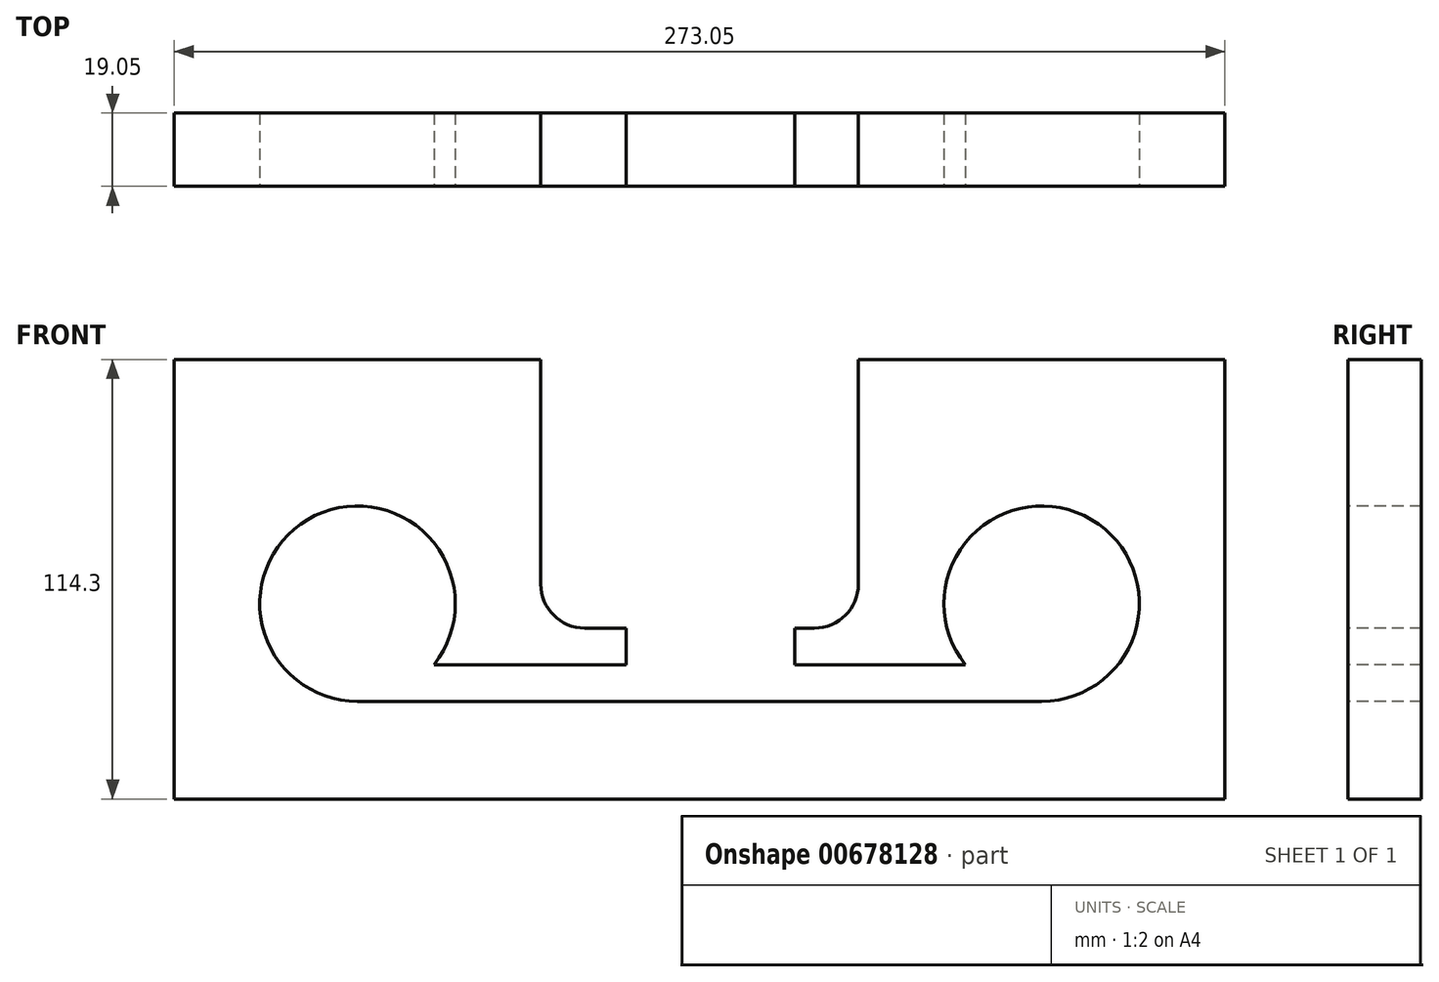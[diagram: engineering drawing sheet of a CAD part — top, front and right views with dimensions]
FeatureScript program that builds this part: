
annotation { "Feature Type Name" : "Feature", "Feature Type Description" : "" }
export const myFeature = defineFeature(function(context is Context, id is Id, definition is map)
    precondition{}
    {
        {
            var Q0;
            Q0=qCreatedBy(makeId("Front.planeOp"),FACE);
            var sketch = newSketch(context, id + "F0", { "sketchPlane" : qUnion([Q0])});
            skLineSegment(sketch, "E0.bottom", {"start": v(0, 0) * mm, "end": v(273.05, 0) * mm});
            skLineSegment(sketch, "E0.top", {"start": v(0, 114.3) * mm, "end": v(273.05, 114.3) * mm});
            skLineSegment(sketch, "E0.left", {"start": v(0, 0) * mm, "end": v(0, 114.3) * mm});
            skLineSegment(sketch, "E0.right", {"start": v(273.05, 0) * mm, "end": v(273.05, 114.3) * mm});
            skSolve(sketch);
        }
        {
            var Q0;
            Q0 = qSketchRegion(id + "F0", true);
            extrude(context, id + "F1", {"entities" : qUnion([Q0]), "depth" : 19.05 * mm, "offsetDistance" : 25.4 * mm});
        }
        {
            var Q0;
            Q0=makeQuery(id+"F1.opExtrude","CAP_FACE",FACE,{"disambiguationData":[OSD([sQuery(id+"F0.wireOp",EDGE,"E0.bottom"),sQuery(id+"F0.wireOp",EDGE,"E0.top"),sQuery(id+"F0.wireOp",EDGE,"E0.left"),sQuery(id+"F0.wireOp",EDGE,"E0.right")])],"isStart":false});
            var sketch = newSketch(context, id + "F2", { "sketchPlane" : qUnion([Q0])});
            skCircle(sketch, "E1", {"center": v(47.63, 50.8) * mm, "radius": 25.4 * mm});
            skCircle(sketch, "E2", {"center": v(225.43, 50.8) * mm, "radius": 25.4 * mm});
            skSolve(sketch);
        }
        {
            var Q0;
            Q0=makeQuery(id+"F2.imprint","IMPRINT",FACE,{"disambiguationData":[TD([[makeQuery(id+"F2.imprint","IMPRINT",EDGE,{"derivedFrom":sQuery(id+"F2.wireOp",EDGE,"E2")}),1.0]])]});
            var Q1;
            Q1=makeQuery(id+"F2.imprint","IMPRINT",FACE,{"disambiguationData":[TD([[makeQuery(id+"F2.imprint","IMPRINT",EDGE,{"derivedFrom":sQuery(id+"F2.wireOp",EDGE,"E1")}),1.0]])]});
            extrude(context, id + "F3", {"entities" : qUnion([Q0, Q1]), "operationType" : NewBodyOperationType.REMOVE, "oppositeDirection" : true, "depth" : 25.4 * mm, "offsetDistance" : 25.4 * mm});
        }
        {
            var Q0;
            Q0=makeQuery(id+"F1.opExtrude","CAP_FACE",FACE,{"disambiguationData":[OSD([sQuery(id+"F0.wireOp",EDGE,"E0.bottom"),sQuery(id+"F0.wireOp",EDGE,"E0.top"),sQuery(id+"F0.wireOp",EDGE,"E0.left"),sQuery(id+"F0.wireOp",EDGE,"E0.right")])],"isStart":false});
            var sketch = newSketch(context, id + "F4", { "sketchPlane" : qUnion([Q0])});
            skLineSegment(sketch, "E3", {"start": v(95.25, 114.3) * mm, "end": v(95.25, 55.88) * mm});
            skLineSegment(sketch, "E4", {"start": v(106.68, 44.45) * mm, "end": v(166.37, 44.45) * mm});
            skLineSegment(sketch, "E5", {"start": v(177.8, 55.88) * mm, "end": v(177.8, 114.3) * mm});
            skPoint(sketch, "E6.visualSharp", {"position": v(95.25, 44.45) * mm});
            skArc(sketch, "E6.filletArc", {"start": v(95.25, 55.88) * mm, "mid": v(98.6, 47.8) * mm, "end": v(106.68, 44.45) * mm});
            skPoint(sketch, "E7.visualSharp", {"position": v(177.8, 44.45) * mm});
            skArc(sketch, "E7.filletArc", {"start": v(166.37, 44.45) * mm, "mid": v(174.45, 47.8) * mm, "end": v(177.8, 55.88) * mm});
            skSolve(sketch);
        }
        {
            var Q0;
            Q0 = qSketchRegion(id + "F4", true);
            var Q1;
            {var subQ1=sQuery(id+"F4.wireOp",EDGE,"E3");Q1=makeQuery(id+"F4.imprint","IMPRINT",FACE,{"disambiguationData":[TD([[makeQuery(id+"F4.imprint","IMPRINT",EDGE,{"derivedFrom":subQ1}),1.0]])]});}
            extrude(context, id + "F5", {"entities" : qUnion([Q0, Q1]), "operationType" : NewBodyOperationType.REMOVE, "oppositeDirection" : true, "depth" : 25.4 * mm, "offsetDistance" : 25.4 * mm});
        }
        {
            var Q0;
            Q0=makeQuery(id+"F1.opExtrude","CAP_FACE",FACE,{"disambiguationData":[OSD([sQuery(id+"F0.wireOp",EDGE,"E0.bottom"),sQuery(id+"F0.wireOp",EDGE,"E0.top"),sQuery(id+"F0.wireOp",EDGE,"E0.left"),sQuery(id+"F0.wireOp",EDGE,"E0.right")])],"isStart":false});
            var sketch = newSketch(context, id + "F6", { "sketchPlane" : qUnion([Q0])});
            skLineSegment(sketch, "E8", {"start": v(67.47, 34.95) * mm, "end": v(47.62, 25.4) * mm});
            skLineSegment(sketch, "E9", {"start": v(47.62, 25.4) * mm, "end": v(225.43, 25.4) * mm});
            skLineSegment(sketch, "E10", {"start": v(225.43, 25.4) * mm, "end": v(205.58, 34.95) * mm});
            skLineSegment(sketch, "E11", {"start": v(205.58, 34.95) * mm, "end": v(166.37, 34.95) * mm});
            skLineSegment(sketch, "E12", {"start": v(67.47, 34.95) * mm, "end": v(117.48, 34.95) * mm});
            skLineSegment(sketch, "E13", {"start": v(117.48, 34.95) * mm, "end": v(117.48, 44.45) * mm});
            skLineSegment(sketch, "E14", {"start": v(117.48, 44.45) * mm, "end": v(161.3, 44.45) * mm});
            skLineSegment(sketch, "E15", {"start": v(161.3, 44.45) * mm, "end": v(161.3, 34.95) * mm});
            skLineSegment(sketch, "E16", {"start": v(161.3, 34.95) * mm, "end": v(166.37, 34.95) * mm});
            skSolve(sketch);
        }
        {
            var Q0;
            Q0 = qSketchRegion(id + "F6", true);
            extrude(context, id + "F7", {"entities" : qUnion([Q0]), "operationType" : NewBodyOperationType.REMOVE, "oppositeDirection" : true, "depth" : 25.4 * mm, "offsetDistance" : 25.4 * mm});
        }
    });
